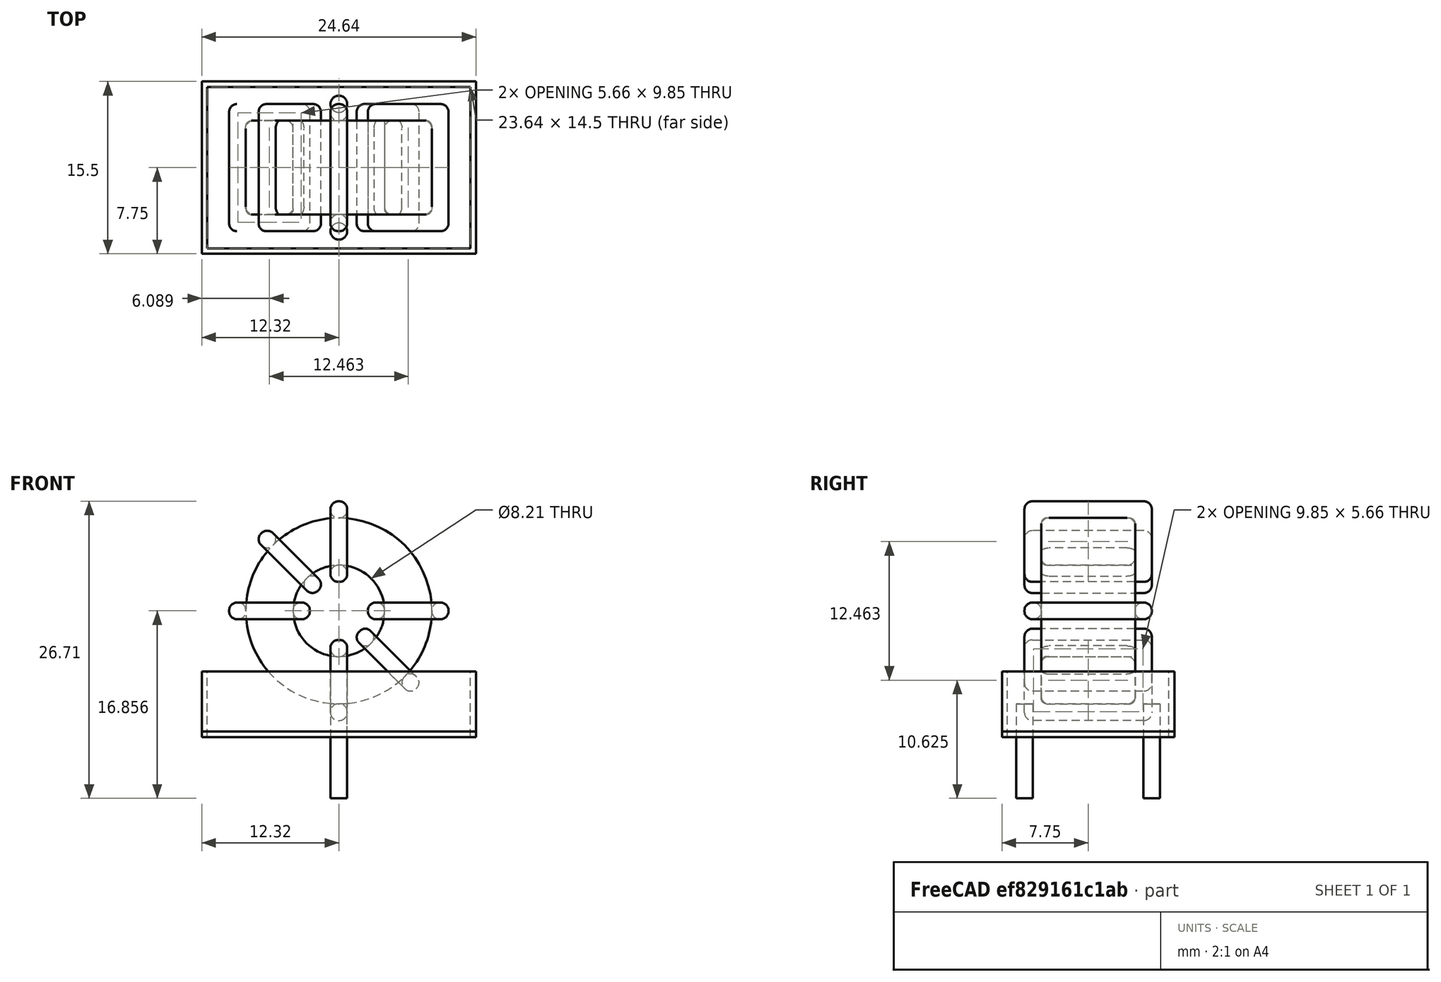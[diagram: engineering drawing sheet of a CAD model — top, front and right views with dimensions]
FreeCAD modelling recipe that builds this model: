
FCSTD DOCUMENT  (FreeCAD 0.16R6703 (Git))
Label: L_Toroid_Vertical_L24.6mm_W15.5mm_P11.44mm_Pulse_KM-4
License: All rights reserved
LicenseURL: http://en.wikipedia.org/wiki/All_rights_reserved
objects: Sketcher::SketchObject×8, PartDesign::Pad×8, PartDesign::Fillet×5, Spreadsheet::Sheet×1
note: 29 computed .brp shape members not serialized (recipe doc carries the construction recipe); baked Part::Feature solids carry a one-line shape summary decoded from their .brp

FEATURE [Spreadsheet::Sheet] Spreadsheet  label="dimensions"
  cells = A1=Wx; B1(Wx)=19.712; C1(WW)=8.213333333333333; D1(iWx)=24.64; A2=Wy; B2(Wy)=11.44; D2(iWy)=15.5; A3=RM; B3(RMx)=11.44; C3(RMy)=0; A4=d_wire; B4(d_wire)=1.5; A5=H; B5(H)=24.64; A6=offsetx; B6(offsetx)=12.32
FEATURE [Sketcher::SketchObject] Sketch
  Placement = pos=(0,-5.72,0) rot=(1,0,0;1.5708rad)
  expr: Placement.Base.y = -Spreadsheet.RMx / 2
  expr: Constraints[0] = Spreadsheet.Wx / 2 - Spreadsheet.d_wire
  expr: Constraints[4] = Spreadsheet.WW / 2
  expr: Constraints[2] = Spreadsheet.Wx / 2 + Spreadsheet.d_wire + 0.5
  sketch-geometry (2):
    g0: Circle CenterX=0 CenterY=11.856 CenterZ=0 NormalX=0 NormalY=0 NormalZ=1 Radius=8.356
    g1: Circle CenterX=0 CenterY=11.856 CenterZ=0 NormalX=0 NormalY=0 NormalZ=1 Radius=4.10667
  constraints (5):
    c: Radius(g0) = 8.356
    c: DistanceX(g-1,g0) = 0
    c: DistanceY(g-1,g0) = 11.856
    c: Coincident(g1,g0)
    c: Radius(g1) = 4.10667
FEATURE [PartDesign::Pad] Pad
  Length = 8.44
  Length2 = 100
  Midplane = true
  Placement = pos=(0,-5.72,0) rot=(1,0,0;1.5708rad)
  Sketch = -> Sketch
  Type = 0
  expr: Length = Spreadsheet.Wy - 2 * Spreadsheet.d_wire
FEATURE [Sketcher::SketchObject] Sketch001
  Placement = pos=(0,0,2) rot=(0,0,1;0rad)
  expr: Placement.Base.z = 0.5 + Spreadsheet.d_wire
  expr: Constraints[4] = Spreadsheet.RMy
  expr: Constraints[2] = -Spreadsheet.RMx
  expr: Constraints[1] = Spreadsheet.d_wire / 2
  sketch-geometry (2):
    g0: Circle CenterX=0 CenterY=0 CenterZ=0 NormalX=0 NormalY=0 NormalZ=1 Radius=0.75
    g1: Circle CenterX=0 CenterY=-11.44 CenterZ=0 NormalX=0 NormalY=0 NormalZ=1 Radius=0.75
  constraints (5):
    c: Equal(g0,g1)
    c: Radius(g0) = 0.75
    c: DistanceY(g-1,g1) = -11.44
    c: Coincident(g0,g-1)
    c: DistanceX(g-1,g1) = 0
FEATURE [PartDesign::Pad] Pad001
  Length = 1.5
  Length2 = 7
  Placement = pos=(0,0,2) rot=(0,0,1;0rad)
  Reversed = true
  Sketch = -> Sketch001
  Type = 4
  expr: Length2 = 5.5 + Spreadsheet.d_wire
  expr: Length = Spreadsheet.d_wire
FEATURE [PartDesign::Fillet] Fillet
  Base = -> Pad [Edge6,Edge3,Edge2]
  Placement = pos=(0,-5.72,0) rot=(1,0,0;1.5708rad)
  Radius = 0.5
FEATURE [Sketcher::SketchObject] Sketch003
  Placement = pos=(0,0,11.856) rot=(1,0,0;3.14159rad)
  expr: Constraints[18] = Spreadsheet.d_wire
  expr: Constraints[16] = Spreadsheet.d_wire
  expr: Constraints[19] = Spreadsheet.d_wire
  expr: Constraints[17] = Spreadsheet.d_wire
  expr: Placement.Base.y = -1 * (Spreadsheet.RMx - Spreadsheet.Wy) / 2
  expr: Constraints[21] = (Spreadsheet.Wx - Spreadsheet.WW) / 2 - Spreadsheet.d_wire
  expr: Constraints[22] = Spreadsheet.Wx / 2 - Spreadsheet.d_wire
  expr: Constraints[43] = Spreadsheet.d_wire
  expr: Constraints[48] = Spreadsheet.Wx - Spreadsheet.d_wire * 2
  expr: Constraints[49] = Spreadsheet.Wy
  expr: Placement.Base.z = Spreadsheet.Wx / 2 + Spreadsheet.d_wire + 0.5
  sketch-geometry (16):
    g0: LineSegment StartX=-2.60667 StartY=0 StartZ=0 EndX=-9.856 EndY=0 EndZ=0
    g1: LineSegment StartX=-9.856 StartY=0 StartZ=0 EndX=-9.856 EndY=11.44 EndZ=0
    g2: LineSegment StartX=-9.856 StartY=11.44 StartZ=0 EndX=-2.60667 EndY=11.44 EndZ=0
    g3: LineSegment StartX=-2.60667 StartY=11.44 StartZ=0 EndX=-2.60667 EndY=0 EndZ=0
    g4: LineSegment StartX=-8.356 StartY=9.94 StartZ=0 EndX=-4.10667 EndY=9.94 EndZ=0
    g5: LineSegment StartX=-4.10667 StartY=9.94 StartZ=0 EndX=-4.10667 EndY=1.5 EndZ=0
    g6: LineSegment StartX=-4.10667 StartY=1.5 StartZ=0 EndX=-8.356 EndY=1.5 EndZ=0
    g7: LineSegment StartX=-8.356 StartY=1.5 StartZ=0 EndX=-8.356 EndY=9.94 EndZ=0
    g8: LineSegment StartX=2.60667 StartY=11.44 StartZ=0 EndX=9.856 EndY=11.44 EndZ=0
    g9: LineSegment StartX=9.856 StartY=11.44 StartZ=0 EndX=9.856 EndY=0 EndZ=0
    g10: LineSegment StartX=9.856 StartY=0 StartZ=0 EndX=2.60667 EndY=0 EndZ=0
    g11: LineSegment StartX=2.60667 StartY=0 StartZ=0 EndX=2.60667 EndY=11.44 EndZ=0
    g12: LineSegment StartX=4.10667 StartY=9.94 StartZ=0 EndX=8.356 EndY=9.94 EndZ=0
    g13: LineSegment StartX=8.356 StartY=9.94 StartZ=0 EndX=8.356 EndY=1.5 EndZ=0
    g14: LineSegment StartX=8.356 StartY=1.5 StartZ=0 EndX=4.10667 EndY=1.5 EndZ=0
    g15: LineSegment StartX=4.10667 StartY=1.5 StartZ=0 EndX=4.10667 EndY=9.94 EndZ=0
  constraints (50):
    c: Horizontal(g0)
    c: Coincident(g1,g0)
    c: Vertical(g1)
    c: Coincident(g2,g1)
    c: Horizontal(g2)
    c: Coincident(g3,g2)
    c: Coincident(g3,g0)
    c: Vertical(g3)
    c: Coincident(g4,g5)
    c: Coincident(g5,g6)
    c: Coincident(g6,g7)
    c: Coincident(g7,g4)
    c: Horizontal(g4)
    c: Horizontal(g6)
    c: Vertical(g5)
    c: Vertical(g7)
    c: DistanceX(g1,g4) = 1.5
    c: DistanceY(g4,g1) = 1.5
    c: DistanceX(g5,g0) = 1.5
    c: DistanceY(g0,g5) = 1.5
    c: DistanceY(g-1,g0) = 0
    c: DistanceX(g6,g6) = 4.24933
    c: DistanceX(g6,g-1) = 8.356
    c: Coincident(g8,g9)
    c: Coincident(g9,g10)
    c: Coincident(g10,g11)
    c: Coincident(g11,g8)
    c: Horizontal(g8)
    c: Horizontal(g10)
    c: Vertical(g9)
    c: Vertical(g11)
    c: Coincident(g12,g13)
    c: Coincident(g13,g14)
    c: Coincident(g14,g15)
    c: Coincident(g15,g12)
    c: Horizontal(g12)
    c: Horizontal(g14)
    c: Vertical(g13)
    c: Vertical(g15)
    c: DistanceY(g8,g2) = 0
    c: DistanceY(g10,g0) = 0
    c: DistanceY(g14,g5) = 0
    c: DistanceY(g12,g4) = 0
    c: DistanceX(g8,g12) = 1.5
    c: Equal(g8,g2)
    c: Equal(g12,g4)
    c: Equal(g9,g1)
    c: Equal(g13,g7)
    c: DistanceX(g4,g12) = 16.712
    c: DistanceY(g0,g1) = 11.44
FEATURE [PartDesign::Pad] Pad002
  Length = 1.5
  Length2 = 100
  Midplane = true
  Placement = pos=(0,0,11.856) rot=(1,0,0;3.14159rad)
  Sketch = -> Sketch003
  Type = 0
  expr: Length = Spreadsheet.d_wire
FEATURE [PartDesign::Fillet] Fillet001
  Base = -> Pad002 [Edge38,Edge41,Edge42,Edge43,Edge29,Edge32,Edge33,Edge34,Edge25,Edge35,Edge36,Edge13,Edge14,Edge15,Edge16,Edge17,Edge18,Edge19,Edge1,Edge2,Edge3,Edge4,Edge5,Edge6,Edge7,Edge37,Edge39,Edge40,Edge20,Edge23,Edge24,Edge21,Edge22,Edge8,Edge9,Edge10,Edge11,Edge12,Edge26,Edge27,+8 more]
  Placement = pos=(0,0,11.856) rot=(1,0,0;3.14159rad)
  Radius = 0.705
  expr: Radius = Spreadsheet.d_wire * 0.47
FEATURE [Sketcher::SketchObject] Sketch004
  Placement = pos=(0,0,11.856) rot=(0.92388,0,0.382683;3.14159rad)
  expr: Constraints[18] = Spreadsheet.d_wire
  expr: Constraints[16] = Spreadsheet.d_wire
  expr: Constraints[19] = Spreadsheet.d_wire
  expr: Constraints[17] = Spreadsheet.d_wire
  expr: Placement.Base.y = -1 * (Spreadsheet.RMx - Spreadsheet.Wy) / 2
  expr: Constraints[21] = (Spreadsheet.Wx - Spreadsheet.WW) / 2 - Spreadsheet.d_wire
  expr: Constraints[22] = Spreadsheet.Wx / 2 - Spreadsheet.d_wire
  expr: Constraints[43] = Spreadsheet.d_wire
  expr: Constraints[48] = Spreadsheet.Wx - 2 * Spreadsheet.d_wire
  expr: Constraints[49] = Spreadsheet.Wy
  expr: Placement.Base.z = Spreadsheet.Wx / 2 + Spreadsheet.d_wire + 0.5
  sketch-geometry (16):
    g0: LineSegment StartX=-2.60667 StartY=0 StartZ=0 EndX=-9.856 EndY=0 EndZ=0
    g1: LineSegment StartX=-9.856 StartY=0 StartZ=0 EndX=-9.856 EndY=11.44 EndZ=0
    g2: LineSegment StartX=-9.856 StartY=11.44 StartZ=0 EndX=-2.60667 EndY=11.44 EndZ=0
    g3: LineSegment StartX=-2.60667 StartY=11.44 StartZ=0 EndX=-2.60667 EndY=0 EndZ=0
    g4: LineSegment StartX=-8.356 StartY=9.94 StartZ=0 EndX=-4.10667 EndY=9.94 EndZ=0
    g5: LineSegment StartX=-4.10667 StartY=9.94 StartZ=0 EndX=-4.10667 EndY=1.5 EndZ=0
    g6: LineSegment StartX=-4.10667 StartY=1.5 StartZ=0 EndX=-8.356 EndY=1.5 EndZ=0
    g7: LineSegment StartX=-8.356 StartY=1.5 StartZ=0 EndX=-8.356 EndY=9.94 EndZ=0
    g8: LineSegment StartX=2.60667 StartY=11.44 StartZ=0 EndX=9.856 EndY=11.44 EndZ=0
    g9: LineSegment StartX=9.856 StartY=11.44 StartZ=0 EndX=9.856 EndY=0 EndZ=0
    g10: LineSegment StartX=9.856 StartY=0 StartZ=0 EndX=2.60667 EndY=0 EndZ=0
    g11: LineSegment StartX=2.60667 StartY=0 StartZ=0 EndX=2.60667 EndY=11.44 EndZ=0
    g12: LineSegment StartX=4.10667 StartY=9.94 StartZ=0 EndX=8.356 EndY=9.94 EndZ=0
    g13: LineSegment StartX=8.356 StartY=9.94 StartZ=0 EndX=8.356 EndY=1.5 EndZ=0
    g14: LineSegment StartX=8.356 StartY=1.5 StartZ=0 EndX=4.10667 EndY=1.5 EndZ=0
    g15: LineSegment StartX=4.10667 StartY=1.5 StartZ=0 EndX=4.10667 EndY=9.94 EndZ=0
  constraints (50):
    c: Horizontal(g0)
    c: Coincident(g1,g0)
    c: Vertical(g1)
    c: Coincident(g2,g1)
    c: Horizontal(g2)
    c: Coincident(g3,g2)
    c: Coincident(g3,g0)
    c: Vertical(g3)
    c: Coincident(g4,g5)
    c: Coincident(g5,g6)
    c: Coincident(g6,g7)
    c: Coincident(g7,g4)
    c: Horizontal(g4)
    c: Horizontal(g6)
    c: Vertical(g5)
    c: Vertical(g7)
    c: DistanceX(g1,g4) = 1.5
    c: DistanceY(g4,g1) = 1.5
    c: DistanceX(g5,g0) = 1.5
    c: DistanceY(g0,g5) = 1.5
    c: DistanceY(g-1,g0) = 0
    c: DistanceX(g6,g6) = 4.24933
    c: DistanceX(g6,g-1) = 8.356
    c: Coincident(g8,g9)
    c: Coincident(g9,g10)
    c: Coincident(g10,g11)
    c: Coincident(g11,g8)
    c: Horizontal(g8)
    c: Horizontal(g10)
    c: Vertical(g9)
    c: Vertical(g11)
    c: Coincident(g12,g13)
    c: Coincident(g13,g14)
    c: Coincident(g14,g15)
    c: Coincident(g15,g12)
    c: Horizontal(g12)
    c: Horizontal(g14)
    c: Vertical(g13)
    c: Vertical(g15)
    c: DistanceY(g8,g2) = 0
    c: DistanceY(g10,g0) = 0
    c: DistanceY(g14,g5) = 0
    c: DistanceY(g12,g4) = 0
    c: DistanceX(g8,g12) = 1.5
    c: Equal(g8,g2)
    c: Equal(g12,g4)
    c: Equal(g9,g1)
    c: Equal(g13,g7)
    c: DistanceX(g4,g12) = 16.712
    c: DistanceY(g0,g1) = 11.44
FEATURE [PartDesign::Pad] Pad003
  Length = 1.5
  Length2 = 100
  Midplane = true
  Placement = pos=(0,0,11.856) rot=(0.92388,0,0.382683;3.14159rad)
  Sketch = -> Sketch004
  Type = 0
  expr: Length = Spreadsheet.d_wire
FEATURE [PartDesign::Fillet] Fillet002
  Base = -> Pad003 [Edge38,Edge41,Edge42,Edge43,Edge29,Edge32,Edge33,Edge34,Edge25,Edge35,Edge36,Edge13,Edge14,Edge15,Edge16,Edge17,Edge18,Edge19,Edge1,Edge2,Edge3,Edge4,Edge5,Edge6,Edge7,Edge37,Edge39,Edge40,Edge20,Edge23,Edge24,Edge21,Edge22,Edge8,Edge9,Edge10,Edge11,Edge12,Edge26,Edge27,+8 more]
  Placement = pos=(0,0,11.856) rot=(0.92388,0,0.382683;3.14159rad)
  Radius = 0.705
  expr: Radius = Spreadsheet.d_wire * 0.47
FEATURE [Sketcher::SketchObject] Sketch005
  Placement = pos=(0,0,11.856) rot=(0.92388,0,-0.382683;3.14159rad)
  expr: Constraints[18] = Spreadsheet.d_wire
  expr: Constraints[16] = Spreadsheet.d_wire
  expr: Constraints[19] = Spreadsheet.d_wire
  expr: Constraints[17] = Spreadsheet.d_wire
  expr: Placement.Base.y = -1 * (Spreadsheet.RMx - Spreadsheet.Wy) / 2
  expr: Constraints[21] = (Spreadsheet.Wx - Spreadsheet.WW) / 2 - Spreadsheet.d_wire
  expr: Constraints[22] = Spreadsheet.Wx / 2 - Spreadsheet.d_wire
  expr: Constraints[43] = Spreadsheet.d_wire
  expr: Constraints[48] = Spreadsheet.Wx - 2 * Spreadsheet.d_wire
  expr: Constraints[49] = Spreadsheet.Wy
  expr: Placement.Base.z = Spreadsheet.Wx / 2 + Spreadsheet.d_wire + 0.5
  sketch-geometry (16):
    g0: LineSegment StartX=-2.60667 StartY=0 StartZ=0 EndX=-9.856 EndY=0 EndZ=0
    g1: LineSegment StartX=-9.856 StartY=0 StartZ=0 EndX=-9.856 EndY=11.44 EndZ=0
    g2: LineSegment StartX=-9.856 StartY=11.44 StartZ=0 EndX=-2.60667 EndY=11.44 EndZ=0
    g3: LineSegment StartX=-2.60667 StartY=11.44 StartZ=0 EndX=-2.60667 EndY=0 EndZ=0
    g4: LineSegment StartX=-8.356 StartY=9.94 StartZ=0 EndX=-4.10667 EndY=9.94 EndZ=0
    g5: LineSegment StartX=-4.10667 StartY=9.94 StartZ=0 EndX=-4.10667 EndY=1.5 EndZ=0
    g6: LineSegment StartX=-4.10667 StartY=1.5 StartZ=0 EndX=-8.356 EndY=1.5 EndZ=0
    g7: LineSegment StartX=-8.356 StartY=1.5 StartZ=0 EndX=-8.356 EndY=9.94 EndZ=0
    g8: LineSegment StartX=2.60667 StartY=11.44 StartZ=0 EndX=9.856 EndY=11.44 EndZ=0
    g9: LineSegment StartX=9.856 StartY=11.44 StartZ=0 EndX=9.856 EndY=0 EndZ=0
    g10: LineSegment StartX=9.856 StartY=0 StartZ=0 EndX=2.60667 EndY=0 EndZ=0
    g11: LineSegment StartX=2.60667 StartY=0 StartZ=0 EndX=2.60667 EndY=11.44 EndZ=0
    g12: LineSegment StartX=4.10667 StartY=9.94 StartZ=0 EndX=8.356 EndY=9.94 EndZ=0
    g13: LineSegment StartX=8.356 StartY=9.94 StartZ=0 EndX=8.356 EndY=1.5 EndZ=0
    g14: LineSegment StartX=8.356 StartY=1.5 StartZ=0 EndX=4.10667 EndY=1.5 EndZ=0
    g15: LineSegment StartX=4.10667 StartY=1.5 StartZ=0 EndX=4.10667 EndY=9.94 EndZ=0
  constraints (50):
    c: Horizontal(g0)
    c: Coincident(g1,g0)
    c: Vertical(g1)
    c: Coincident(g2,g1)
    c: Horizontal(g2)
    c: Coincident(g3,g2)
    c: Coincident(g3,g0)
    c: Vertical(g3)
    c: Coincident(g4,g5)
    c: Coincident(g5,g6)
    c: Coincident(g6,g7)
    c: Coincident(g7,g4)
    c: Horizontal(g4)
    c: Horizontal(g6)
    c: Vertical(g5)
    c: Vertical(g7)
    c: DistanceX(g1,g4) = 1.5
    c: DistanceY(g4,g1) = 1.5
    c: DistanceX(g5,g0) = 1.5
    c: DistanceY(g0,g5) = 1.5
    c: DistanceY(g-1,g0) = 0
    c: DistanceX(g6,g6) = 4.24933
    c: DistanceX(g6,g-1) = 8.356
    c: Coincident(g8,g9)
    c: Coincident(g9,g10)
    c: Coincident(g10,g11)
    c: Coincident(g11,g8)
    c: Horizontal(g8)
    c: Horizontal(g10)
    c: Vertical(g9)
    c: Vertical(g11)
    c: Coincident(g12,g13)
    c: Coincident(g13,g14)
    c: Coincident(g14,g15)
    c: Coincident(g15,g12)
    c: Horizontal(g12)
    c: Horizontal(g14)
    c: Vertical(g13)
    c: Vertical(g15)
    c: DistanceY(g8,g2) = 0
    c: DistanceY(g10,g0) = 0
    c: DistanceY(g14,g5) = 0
    c: DistanceY(g12,g4) = 0
    c: DistanceX(g8,g12) = 1.5
    c: Equal(g8,g2)
    c: Equal(g12,g4)
    c: Equal(g9,g1)
    c: Equal(g13,g7)
    c: DistanceX(g4,g12) = 16.712
    c: DistanceY(g0,g1) = 11.44
FEATURE [PartDesign::Pad] Pad004
  Length = 1.5
  Length2 = 100
  Midplane = true
  Placement = pos=(0,0,11.856) rot=(0.92388,0,-0.382683;3.14159rad)
  Sketch = -> Sketch005
  Type = 0
  expr: Length = Spreadsheet.d_wire
FEATURE [PartDesign::Fillet] Fillet003
  Base = -> Pad004 [Edge38,Edge41,Edge42,Edge43,Edge29,Edge32,Edge33,Edge34,Edge25,Edge35,Edge36,Edge13,Edge14,Edge15,Edge16,Edge17,Edge18,Edge19,Edge1,Edge2,Edge3,Edge4,Edge5,Edge6,Edge7,Edge37,Edge39,Edge40,Edge20,Edge23,Edge24,Edge21,Edge22,Edge8,Edge9,Edge10,Edge11,Edge12,Edge26,Edge27,+8 more]
  Placement = pos=(0,0,11.856) rot=(0.92388,0,-0.382683;3.14159rad)
  Radius = 0.705
  expr: Radius = Spreadsheet.d_wire * 0.47
FEATURE [Sketcher::SketchObject] Sketch006
  Placement = pos=(0,0,11.856) rot=(0.707107,0,0.707107;3.14159rad)
  expr: Constraints[18] = Spreadsheet.d_wire
  expr: Constraints[16] = Spreadsheet.d_wire
  expr: Constraints[19] = Spreadsheet.d_wire
  expr: Constraints[17] = Spreadsheet.d_wire
  expr: Placement.Base.y = -1 * (Spreadsheet.RMx - Spreadsheet.Wy) / 2
  expr: Constraints[21] = (Spreadsheet.Wx - Spreadsheet.WW) / 2 - Spreadsheet.d_wire
  expr: Constraints[22] = Spreadsheet.Wx / 2 - Spreadsheet.d_wire
  expr: Constraints[43] = Spreadsheet.d_wire
  expr: Constraints[48] = Spreadsheet.Wx - Spreadsheet.d_wire * 2
  expr: Constraints[49] = Spreadsheet.Wy
  expr: Placement.Base.z = Spreadsheet.Wx / 2 + Spreadsheet.d_wire + 0.5
  sketch-geometry (16):
    g0: LineSegment StartX=-2.60667 StartY=0 StartZ=0 EndX=-9.856 EndY=0 EndZ=0
    g1: LineSegment StartX=-9.856 StartY=0 StartZ=0 EndX=-9.856 EndY=11.44 EndZ=0
    g2: LineSegment StartX=-9.856 StartY=11.44 StartZ=0 EndX=-2.60667 EndY=11.44 EndZ=0
    g3: LineSegment StartX=-2.60667 StartY=11.44 StartZ=0 EndX=-2.60667 EndY=0 EndZ=0
    g4: LineSegment StartX=-8.356 StartY=9.94 StartZ=0 EndX=-4.10667 EndY=9.94 EndZ=0
    g5: LineSegment StartX=-4.10667 StartY=9.94 StartZ=0 EndX=-4.10667 EndY=1.5 EndZ=0
    g6: LineSegment StartX=-4.10667 StartY=1.5 StartZ=0 EndX=-8.356 EndY=1.5 EndZ=0
    g7: LineSegment StartX=-8.356 StartY=1.5 StartZ=0 EndX=-8.356 EndY=9.94 EndZ=0
    g8: LineSegment StartX=2.60667 StartY=11.44 StartZ=0 EndX=9.856 EndY=11.44 EndZ=0
    g9: LineSegment StartX=9.856 StartY=11.44 StartZ=0 EndX=9.856 EndY=0 EndZ=0
    g10: LineSegment StartX=9.856 StartY=0 StartZ=0 EndX=2.60667 EndY=0 EndZ=0
    g11: LineSegment StartX=2.60667 StartY=0 StartZ=0 EndX=2.60667 EndY=11.44 EndZ=0
    g12: LineSegment StartX=4.10667 StartY=9.94 StartZ=0 EndX=8.356 EndY=9.94 EndZ=0
    g13: LineSegment StartX=8.356 StartY=9.94 StartZ=0 EndX=8.356 EndY=1.5 EndZ=0
    g14: LineSegment StartX=8.356 StartY=1.5 StartZ=0 EndX=4.10667 EndY=1.5 EndZ=0
    g15: LineSegment StartX=4.10667 StartY=1.5 StartZ=0 EndX=4.10667 EndY=9.94 EndZ=0
  constraints (50):
    c: Horizontal(g0)
    c: Coincident(g1,g0)
    c: Vertical(g1)
    c: Coincident(g2,g1)
    c: Horizontal(g2)
    c: Coincident(g3,g2)
    c: Coincident(g3,g0)
    c: Vertical(g3)
    c: Coincident(g4,g5)
    c: Coincident(g5,g6)
    c: Coincident(g6,g7)
    c: Coincident(g7,g4)
    c: Horizontal(g4)
    c: Horizontal(g6)
    c: Vertical(g5)
    c: Vertical(g7)
    c: DistanceX(g1,g4) = 1.5
    c: DistanceY(g4,g1) = 1.5
    c: DistanceX(g5,g0) = 1.5
    c: DistanceY(g0,g5) = 1.5
    c: DistanceY(g-1,g0) = 0
    c: DistanceX(g6,g6) = 4.24933
    c: DistanceX(g6,g-1) = 8.356
    c: Coincident(g8,g9)
    c: Coincident(g9,g10)
    c: Coincident(g10,g11)
    c: Coincident(g11,g8)
    c: Horizontal(g8)
    c: Horizontal(g10)
    c: Vertical(g9)
    c: Vertical(g11)
    c: Coincident(g12,g13)
    c: Coincident(g13,g14)
    c: Coincident(g14,g15)
    c: Coincident(g15,g12)
    c: Horizontal(g12)
    c: Horizontal(g14)
    c: Vertical(g13)
    c: Vertical(g15)
    c: DistanceY(g8,g2) = 0
    c: DistanceY(g10,g0) = 0
    c: DistanceY(g14,g5) = 0
    c: DistanceY(g12,g4) = 0
    c: DistanceX(g8,g12) = 1.5
    c: Equal(g8,g2)
    c: Equal(g12,g4)
    c: Equal(g9,g1)
    c: Equal(g13,g7)
    c: DistanceX(g4,g12) = 16.712
    c: DistanceY(g0,g1) = 11.44
FEATURE [PartDesign::Pad] Pad005
  Length = 1.5
  Length2 = 100
  Midplane = true
  Placement = pos=(0,0,11.856) rot=(0.707107,0,0.707107;3.14159rad)
  Sketch = -> Sketch006
  Type = 0
  expr: Length = Spreadsheet.d_wire
FEATURE [PartDesign::Fillet] Fillet004
  Base = -> Pad005 [Edge38,Edge41,Edge42,Edge43,Edge29,Edge32,Edge33,Edge34,Edge25,Edge35,Edge36,Edge13,Edge14,Edge15,Edge16,Edge17,Edge18,Edge19,Edge1,Edge2,Edge3,Edge4,Edge5,Edge6,Edge7,Edge37,Edge39,Edge40,Edge20,Edge23,Edge24,Edge21,Edge22,Edge8,Edge9,Edge10,Edge11,Edge12,Edge26,Edge27,+8 more]
  Placement = pos=(0,0,11.856) rot=(0.707107,0,0.707107;3.14159rad)
  Radius = 0.705
  expr: Radius = Spreadsheet.d_wire * 0.47
FEATURE [Sketcher::SketchObject] Sketch007
  Placement = pos=(0,0,0.5) rot=(0,0,1;0rad)
  expr: Placement.Base.z = 0.5
  expr: Constraints[11] = Spreadsheet.iWx / 2
  expr: Constraints[10] = (Spreadsheet.iWy - Spreadsheet.RMx) / 2
  expr: Constraints[9] = Spreadsheet.iWy
  expr: Constraints[8] = Spreadsheet.iWx
  sketch-geometry (4):
    g0: LineSegment StartX=-12.32 StartY=2.03 StartZ=0 EndX=12.32 EndY=2.03 EndZ=0
    g1: LineSegment StartX=12.32 StartY=2.03 StartZ=0 EndX=12.32 EndY=-13.47 EndZ=0
    g2: LineSegment StartX=12.32 StartY=-13.47 StartZ=0 EndX=-12.32 EndY=-13.47 EndZ=0
    g3: LineSegment StartX=-12.32 StartY=-13.47 StartZ=0 EndX=-12.32 EndY=2.03 EndZ=0
  constraints (12):
    c: Coincident(g0,g1)
    c: Coincident(g1,g2)
    c: Coincident(g2,g3)
    c: Coincident(g3,g0)
    c: Horizontal(g0)
    c: Horizontal(g2)
    c: Vertical(g1)
    c: Vertical(g3)
    c: DistanceX(g0,g0) = 24.64
    c: DistanceY(g3,g3) = 15.5
    c: DistanceY(g-1,g0) = 2.03
    c: DistanceX(g0,g-1) = 12.32
FEATURE [PartDesign::Pad] Pad006
  Length = 0.5
  Length2 = 100
  Placement = pos=(0,0,0.5) rot=(0,0,1;0rad)
  Sketch = -> Sketch007
  Type = 0
FEATURE [Sketcher::SketchObject] Sketch008
  Placement = pos=(0,0,0.5) rot=(0,0,1;0rad)
  expr: Constraints[8] = Spreadsheet.iWx
  expr: Constraints[9] = Spreadsheet.iWy
  expr: Constraints[10] = (Spreadsheet.iWy - Spreadsheet.RMx) / 2
  expr: Placement.Base.z = 0.5
  expr: Constraints[21] = 0.5
  expr: Constraints[11] = Spreadsheet.iWx / 2
  sketch-geometry (8):
    g0: LineSegment StartX=-12.32 StartY=2.03 StartZ=0 EndX=12.32 EndY=2.03 EndZ=0
    g1: LineSegment StartX=12.32 StartY=2.03 StartZ=0 EndX=12.32 EndY=-13.47 EndZ=0
    g2: LineSegment StartX=12.32 StartY=-13.47 StartZ=0 EndX=-12.32 EndY=-13.47 EndZ=0
    g3: LineSegment StartX=-12.32 StartY=-13.47 StartZ=0 EndX=-12.32 EndY=2.03 EndZ=0
    g4: LineSegment StartX=-11.82 StartY=1.53 StartZ=0 EndX=11.82 EndY=1.53 EndZ=0
    g5: LineSegment StartX=11.82 StartY=1.53 StartZ=0 EndX=11.82 EndY=-12.97 EndZ=0
    g6: LineSegment StartX=11.82 StartY=-12.97 StartZ=0 EndX=-11.82 EndY=-12.97 EndZ=0
    g7: LineSegment StartX=-11.82 StartY=-12.97 StartZ=0 EndX=-11.82 EndY=1.53 EndZ=0
  constraints (24):
    c: Coincident(g0,g1)
    c: Coincident(g1,g2)
    c: Coincident(g2,g3)
    c: Coincident(g3,g0)
    c: Horizontal(g0)
    c: Horizontal(g2)
    c: Vertical(g1)
    c: Vertical(g3)
    c: DistanceX(g0,g0) = 24.64
    c: DistanceY(g3,g3) = 15.5
    c: DistanceY(g-1,g0) = 2.03
    c: DistanceX(g0,g-1) = 12.32
    c: Coincident(g4,g5)
    c: Coincident(g5,g6)
    c: Coincident(g6,g7)
    c: Coincident(g7,g4)
    c: Horizontal(g4)
    c: Horizontal(g6)
    c: Vertical(g5)
    c: Vertical(g7)
    c: DistanceX(g5,g1) = 0.5
    c: DistanceY(g1,g5) = 0.5
    c: DistanceX(g0,g4) = 0.5
    c: DistanceY(g4,g0) = 0.5
FEATURE [PartDesign::Pad] Pad007
  Length = 5.9136
  Length2 = 100
  Placement = pos=(0,0,0.5) rot=(0,0,1;0rad)
  Sketch = -> Sketch008
  Type = 0
  expr: Length = Spreadsheet.Wx * 0.3
